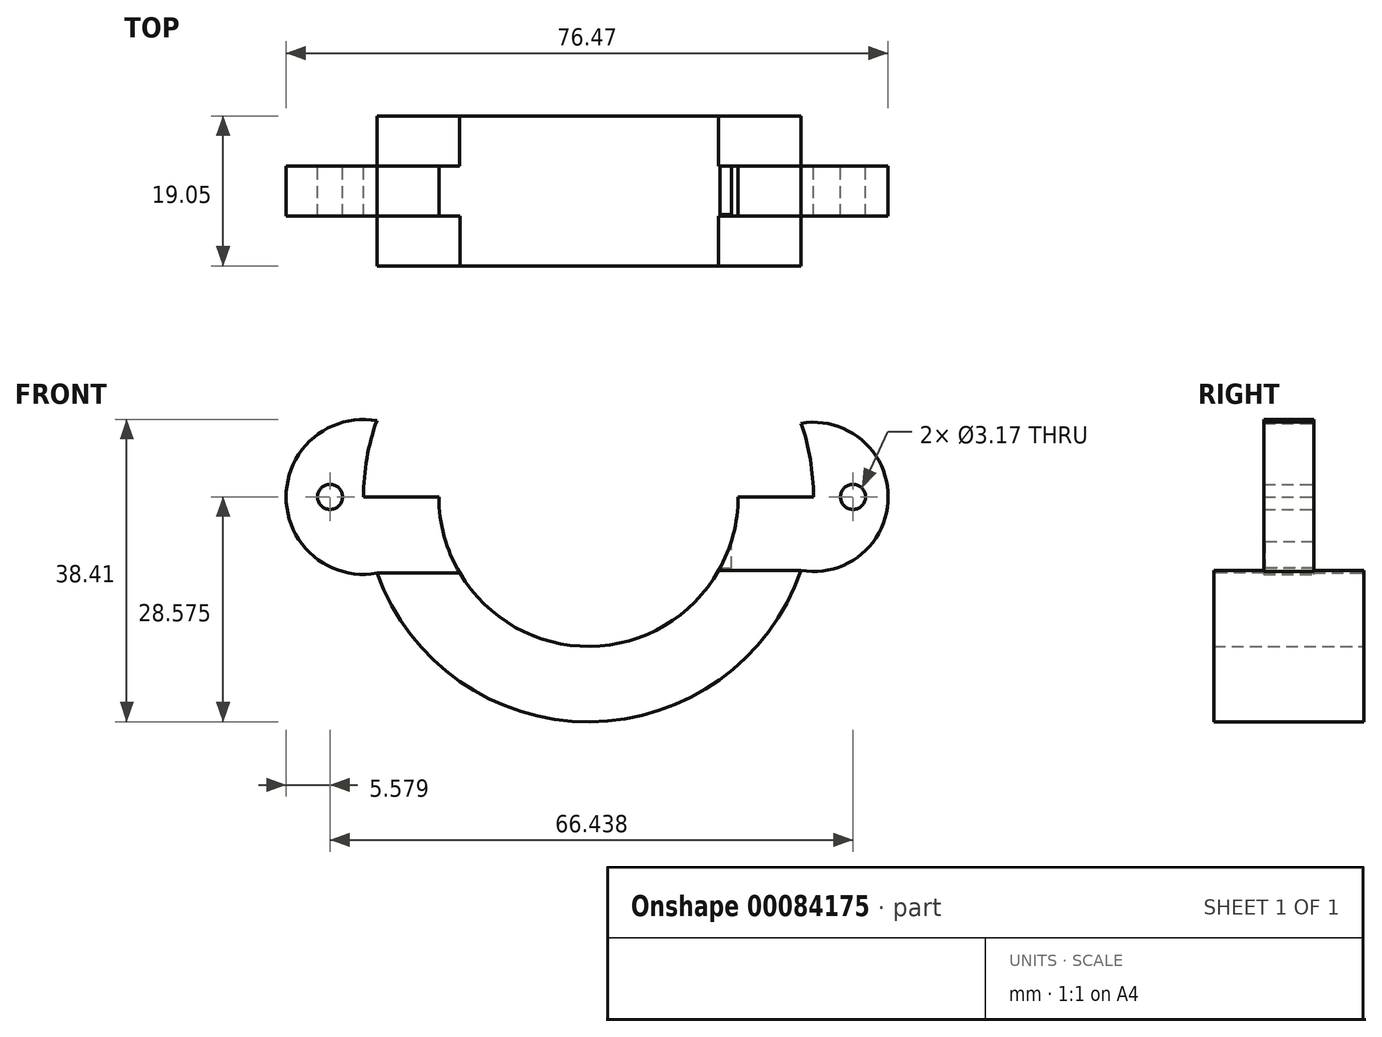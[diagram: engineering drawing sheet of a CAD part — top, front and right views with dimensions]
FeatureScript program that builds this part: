
annotation { "Feature Type Name" : "Feature", "Feature Type Description" : "" }
export const myFeature = defineFeature(function(context is Context, id is Id, definition is map)
    precondition{}
    {
        {
            var Q0;
            Q0=qCreatedBy(makeId("Front.planeOp"),FACE);
            var sketch = newSketch(context, id + "F0", { "sketchPlane" : qUnion([Q0])});
            skArc(sketch, "E0", {"start": v(-34.77, 27.01) * mm, "mid": v(-15.77, 8.01) * mm, "end": v(3.23, 27.01) * mm});
            skArc(sketch, "E1", {"start": v(-42.65, 36.7) * mm, "mid": v(-43.92, 31.93) * mm, "end": v(-44.34, 27.01) * mm});
            skArc(sketch, "E2", {"start": v(-42.65, 36.7) * mm, "mid": v(-54.18, 27.01) * mm, "end": v(-42.65, 17.32) * mm});
            skArc(sketch, "E3", {"start": v(11.23, 17.66) * mm, "mid": v(22.29, 27.01) * mm, "end": v(11.23, 36.37) * mm});
            skCircle(sketch, "E4", {"center": v(-48.6, 27.01) * mm, "radius": 1.59 * mm});
            skPoint(sketch, "E4.centerSnap0", {"position": v(-54.18, 27.01) * mm});
            skCircle(sketch, "E5", {"center": v(17.84, 27.01) * mm, "radius": 1.59 * mm});
            skLineSegment(sketch, "E6", {"start": v(-44.34, 27.01) * mm, "end": v(-34.77, 27.01) * mm});
            skLineSegment(sketch, "E7", {"start": v(3.23, 27.01) * mm, "end": v(12.8, 27.01) * mm});
            skArc(sketch, "E8.trimOffspring", {"start": v(-42.65, 17.32) * mm, "mid": v(-15.59, -1.56) * mm, "end": v(11.23, 17.66) * mm});
            skArc(sketch, "E9.trimOffspring", {"start": v(12.8, 27.01) * mm, "mid": v(12.4, 31.76) * mm, "end": v(11.23, 36.37) * mm});
            skSolve(sketch);
        }
        {
            var Q0;
            Q0=qSketchRegion(id+"F0",true);
            extrude(context, id + "F1", {"entities" : qUnion([Q0]), "depth" : 19.05 * mm});
        }
        {
            var Q0;
            Q0=makeQuery(id+"F1.opExtrude","CAP_FACE",FACE,{"disambiguationData":[OSD([sQuery(id+"F0.wireOp",EDGE,"E0"),sQuery(id+"F0.wireOp",EDGE,"E1"),sQuery(id+"F0.wireOp",EDGE,"E2"),sQuery(id+"F0.wireOp",EDGE,"E3"),sQuery(id+"F0.wireOp",EDGE,"E4"),sQuery(id+"F0.wireOp",EDGE,"E5"),sQuery(id+"F0.wireOp",EDGE,"E6"),sQuery(id+"F0.wireOp",EDGE,"E7"),sQuery(id+"F0.wireOp",EDGE,"E8.trimOffspring"),sQuery(id+"F0.wireOp",EDGE,"E9.trimOffspring")])],"isStart":false});
            var sketch = newSketch(context, id + "F2", { "sketchPlane" : qUnion([Q0])});
            skLineSegment(sketch, "E10", {"start": v(-42.65, 17.32) * mm, "end": v(-32.11, 17.32) * mm});
            skLineSegment(sketch, "E11", {"start": v(11.23, 17.66) * mm, "end": v(0.77, 17.66) * mm});
            skSolve(sketch);
        }
        {
            var Q0;
            Q0 = qSketchRegion(id + "F2", true);
            var Q1;
            {var subQ2=sQuery(id+"F2.wireOp",EDGE,"E10");Q1=makeQuery(id+"F2.imprint","IMPRINT",FACE,{"disambiguationData":[TD([[makeQuery(id+"F2.imprint","IMPRINT",EDGE,{"derivedFrom":subQ2}),1.0]])]});}
            var Q2;
            {var subQ1=sQuery(id+"F2.wireOp",EDGE,"E11");Q2=makeQuery(id+"F2.imprint","IMPRINT",FACE,{"disambiguationData":[TD([[makeQuery(id+"F2.imprint","IMPRINT",EDGE,{"derivedFrom":subQ1}),-1.0]])]});}
            extrude(context, id + "F3", {"entities" : qUnion([Q0, Q1, Q2]), "operationType" : NewBodyOperationType.REMOVE, "oppositeDirection" : true, "depth" : 6.35 * mm});
        }
        {
            var Q0;
            Q0=makeQuery(id+"F1.opExtrude","CAP_FACE",FACE,{"disambiguationData":[OSD([sQuery(id+"F0.wireOp",EDGE,"E0"),sQuery(id+"F0.wireOp",EDGE,"E1"),sQuery(id+"F0.wireOp",EDGE,"E2"),sQuery(id+"F0.wireOp",EDGE,"E3"),sQuery(id+"F0.wireOp",EDGE,"E4"),sQuery(id+"F0.wireOp",EDGE,"E5"),sQuery(id+"F0.wireOp",EDGE,"E6"),sQuery(id+"F0.wireOp",EDGE,"E7"),sQuery(id+"F0.wireOp",EDGE,"E8.trimOffspring"),sQuery(id+"F0.wireOp",EDGE,"E9.trimOffspring")])],"isStart":true});
            var sketch = newSketch(context, id + "F4", { "sketchPlane" : qUnion([Q0])});
            skLineSegment(sketch, "E12", {"start": v(-11.23, 17.66) * mm, "end": v(-0.77, 17.66) * mm});
            skLineSegment(sketch, "E13", {"start": v(42.65, 17.32) * mm, "end": v(32.13, 17.36) * mm});
            skSolve(sketch);
        }
        {
            var Q0;
            Q0 = qSketchRegion(id + "F4", true);
            var Q1;
            {var subQ1=sQuery(id+"F4.wireOp",EDGE,"E12");Q1=makeQuery(id+"F4.imprint","IMPRINT",FACE,{"disambiguationData":[TD([[makeQuery(id+"F4.imprint","IMPRINT",EDGE,{"derivedFrom":subQ1}),1.0]])]});}
            var Q2;
            {var subQ0=sQuery(id+"F4.wireOp",EDGE,"E13");Q2=makeQuery(id+"F4.imprint","IMPRINT",FACE,{"disambiguationData":[TD([[makeQuery(id+"F4.imprint","IMPRINT",EDGE,{"derivedFrom":subQ0}),-1.0]])]});}
            extrude(context, id + "F5", {"entities" : qUnion([Q0, Q1, Q2]), "operationType" : NewBodyOperationType.REMOVE, "oppositeDirection" : true, "depth" : 6.35 * mm});
        }
        {
            var Q0;
            Q0=makeQuery(id+"F5.boolean.opBoolean","COPY",FACE,{"derivedFrom":makeQuery(id+"F5.opExtrude","SWEPT_FACE",FACE,{"disambiguationData":[OSD([sQuery(id+"F4.wireOp",EDGE,"E13")])]})});
            cPlane(context, id + "F6", {"entities" : qUnion([Q0]), "cplaneType" : CPlaneType.OFFSET, "offset" : 152.4 * mm, "width" : 152.4 * mm, "height" : 152.4 * mm});
        }
        {
            var Q0;
            Q0=qCreatedBy(id+"F6.planeOp",FACE);
            var sketch = newSketch(context, id + "F7", { "sketchPlane" : qUnion([Q0])});
            skLineSegment(sketch, "E14", {"start": v(-31.67, -5.82) * mm, "end": v(2.45, -5.82) * mm});
            skLineSegment(sketch, "E15", {"start": v(2.45, -5.82) * mm, "end": v(2.45, -12.53) * mm});
            skLineSegment(sketch, "E16", {"start": v(2.45, -12.53) * mm, "end": v(-31.37, -12.53) * mm});
            skLineSegment(sketch, "E17", {"start": v(-31.37, -12.53) * mm, "end": v(-31.67, -5.82) * mm});
            skSolve(sketch);
        }
        {
            var Q0;
            Q0 = qSketchRegion(id + "F7", true);
            extrude(context, id + "F8", {"entities" : qUnion([Q0]), "operationType" : NewBodyOperationType.REMOVE, "oppositeDirection" : true, "depth" : 151.92 * mm});
        }
    });
